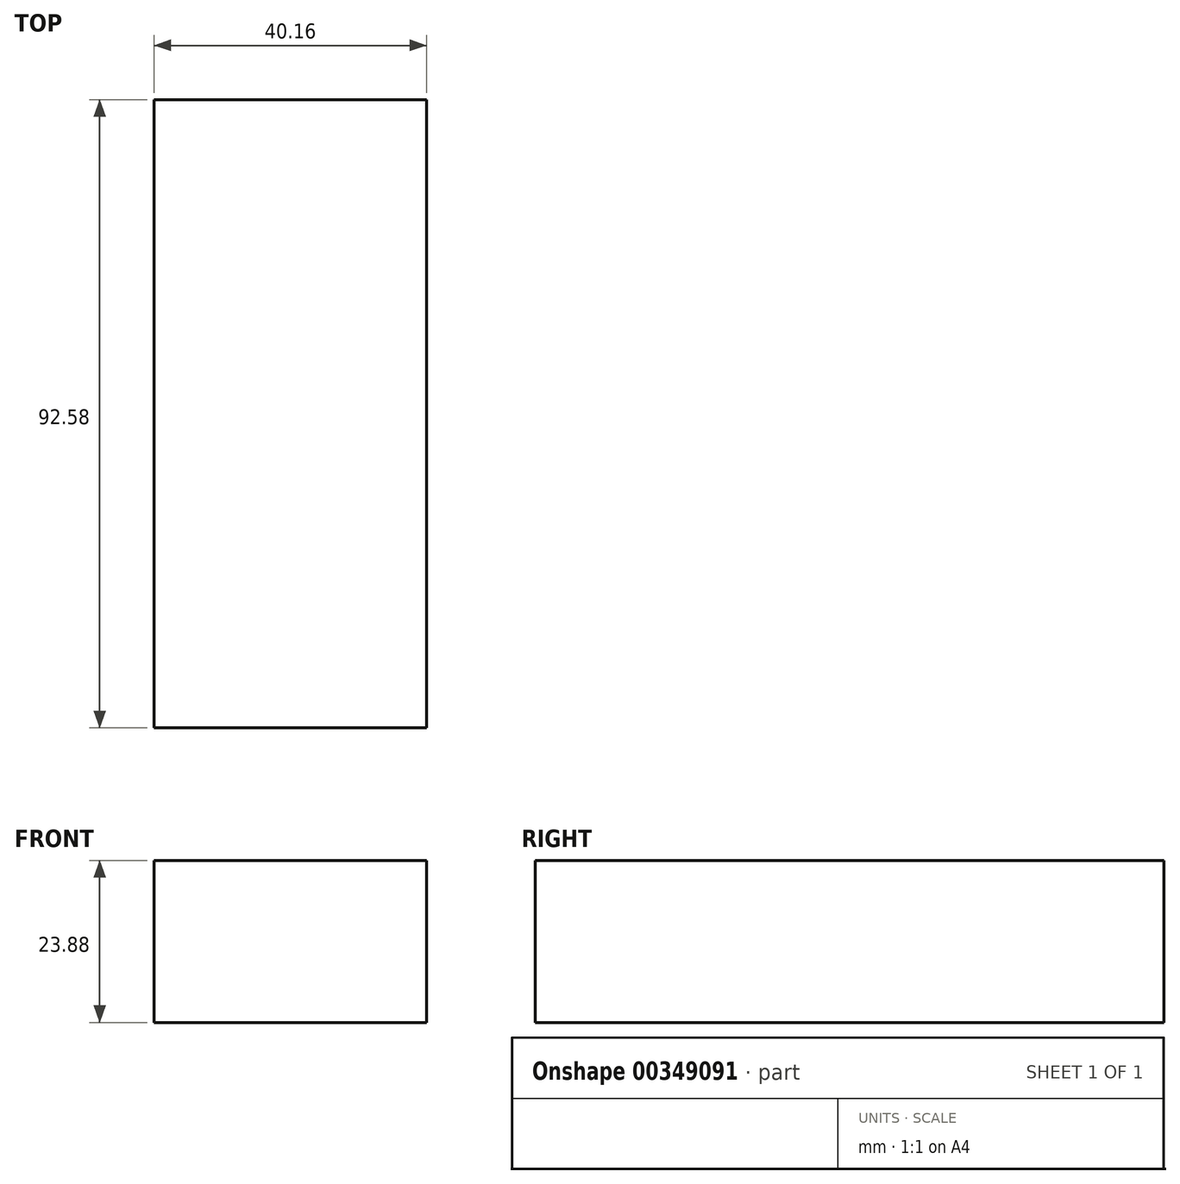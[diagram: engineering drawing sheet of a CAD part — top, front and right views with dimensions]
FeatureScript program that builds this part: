
annotation { "Feature Type Name" : "Feature", "Feature Type Description" : "" }
export const myFeature = defineFeature(function(context is Context, id is Id, definition is map)
    precondition{}
    {
        {
            var Q0;
            Q0=qCreatedBy(makeId("Top.planeOp"),FACE);
            var sketch = newSketch(context, id + "F0", { "sketchPlane" : qUnion([Q0])});
            skLineSegment(sketch, "E0.bottom", {"start": v(0, 46.29) * mm, "end": v(-40.16, 46.29) * mm});
            skLineSegment(sketch, "E0.top", {"start": v(0, -46.29) * mm, "end": v(-40.16, -46.29) * mm});
            skLineSegment(sketch, "E0.left", {"start": v(0, 46.29) * mm, "end": v(0, -46.29) * mm});
            skLineSegment(sketch, "E0.right", {"start": v(-40.16, 46.29) * mm, "end": v(-40.16, -46.29) * mm});
            skSolve(sketch);
        }
        {
            var Q0;
            Q0=makeQuery(id+"F0.imprint","IMPRINT",FACE,{"disambiguationData":[TD([[makeQuery(id+"F0.imprint","IMPRINT",EDGE,{"derivedFrom":sQuery(id+"F0.wireOp",EDGE,"E0.bottom")}),1.0]])]});
            extrude(context, id + "F1", {"entities" : qUnion([Q0]), "depth" : 23.88 * mm});
        }
    });
